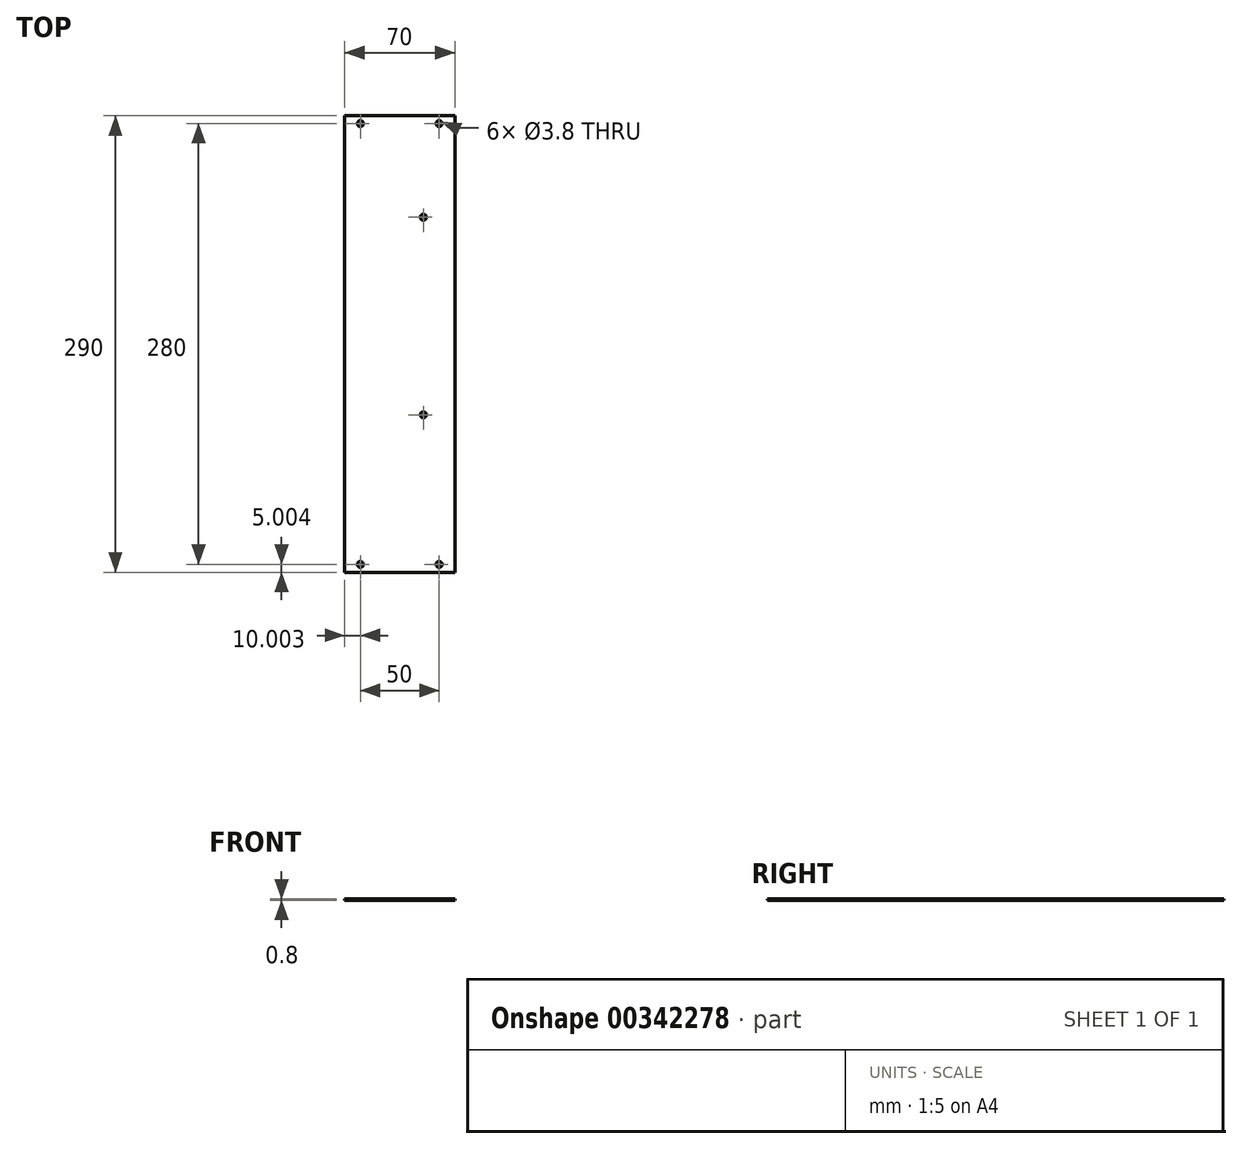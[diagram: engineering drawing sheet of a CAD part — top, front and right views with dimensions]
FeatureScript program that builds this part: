
annotation { "Feature Type Name" : "Feature", "Feature Type Description" : "" }
export const myFeature = defineFeature(function(context is Context, id is Id, definition is map)
    precondition{}
    {
        {
            var Q0;
            Q0=qCreatedBy(makeId("Top.planeOp"),FACE);
            var sketch = newSketch(context, id + "F0", { "sketchPlane" : qUnion([Q0])});
            skLineSegment(sketch, "E0.bottom", {"start": v(-107.73, 102.93) * mm, "end": v(-37.73, 102.93) * mm});
            skLineSegment(sketch, "E0.top", {"start": v(-107.73, -187.07) * mm, "end": v(-37.73, -187.07) * mm});
            skLineSegment(sketch, "E0.left", {"start": v(-107.73, 102.93) * mm, "end": v(-107.73, -187.07) * mm});
            skLineSegment(sketch, "E0.right", {"start": v(-37.73, 102.93) * mm, "end": v(-37.73, -187.07) * mm});
            skCircle(sketch, "E1", {"center": v(-57.73, -87.07) * mm, "radius": 1.9 * mm});
            skCircle(sketch, "E2", {"center": v(-57.73, 38.43) * mm, "radius": 1.9 * mm});
            skCircle(sketch, "E3", {"center": v(-97.73, 97.93) * mm, "radius": 1.9 * mm});
            skCircle(sketch, "E4", {"center": v(-47.73, 97.93) * mm, "radius": 1.9 * mm});
            skCircle(sketch, "E5", {"center": v(-97.73, -182.07) * mm, "radius": 1.9 * mm});
            skCircle(sketch, "E6", {"center": v(-47.73, -182.07) * mm, "radius": 1.9 * mm});
            skSolve(sketch);
        }
        {
            var Q0;
            Q0=makeQuery(id+"F0.imprint","IMPRINT",FACE,{"disambiguationData":[TD([[makeQuery(id+"F0.imprint","IMPRINT",EDGE,{"derivedFrom":sQuery(id+"F0.wireOp",EDGE,"E0.bottom")}),-1.0]])]});
            extrude(context, id + "F1", {"entities" : qUnion([Q0]), "depth" : 0.8 * mm});
        }
    });
